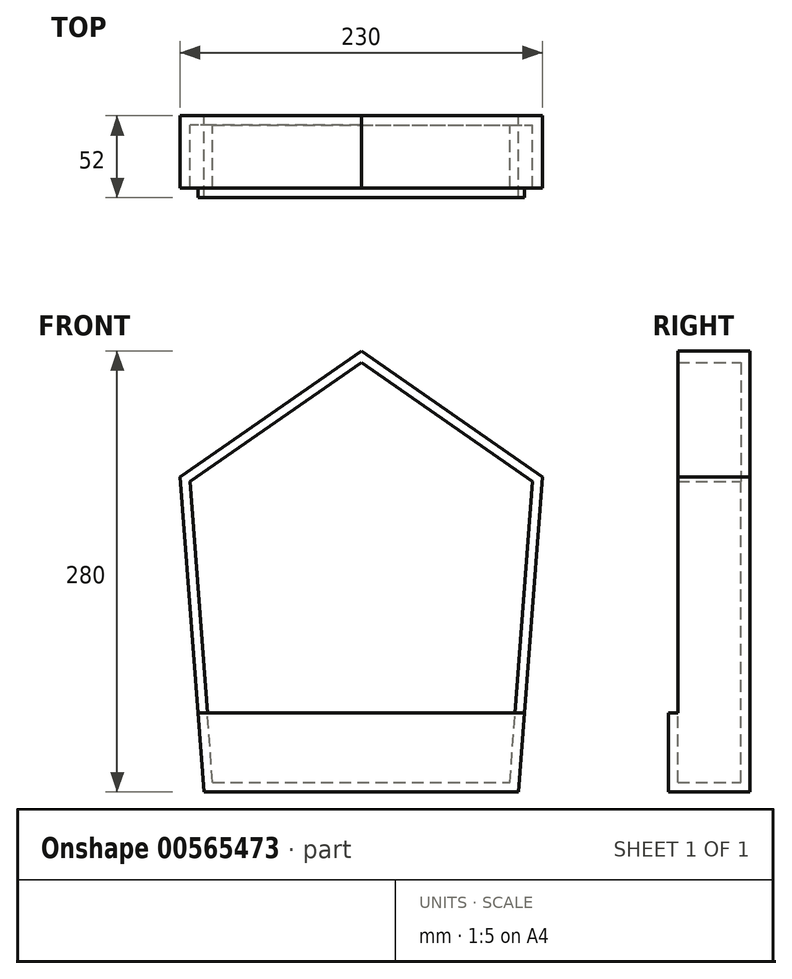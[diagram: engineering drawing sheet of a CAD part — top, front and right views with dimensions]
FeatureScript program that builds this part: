
annotation { "Feature Type Name" : "Feature", "Feature Type Description" : "" }
export const myFeature = defineFeature(function(context is Context, id is Id, definition is map)
    precondition{}
    {
        {
            var Q0;
            Q0=qCreatedBy(makeId("Front.planeOp"),FACE);
            var sketch = newSketch(context, id + "F0", { "sketchPlane" : qUnion([Q0])});
            skLineSegment(sketch, "E0.bottom", {"start": v(0, 0) * mm, "end": v(200, 0) * mm});
            skLineSegment(sketch, "E0.top", {"start": v(-15, 200) * mm, "end": v(215, 200) * mm});
            skLineSegment(sketch, "E0.left", {"start": v(0, 0) * mm, "end": v(-15, 200) * mm});
            skLineSegment(sketch, "E0.right", {"start": v(200, 0) * mm, "end": v(215, 200) * mm});
            skLineSegment(sketch, "E1", {"start": v(-15, 200) * mm, "end": v(100, 200) * mm});
            skLineSegment(sketch, "E2", {"start": v(100, 200) * mm, "end": v(100, 280) * mm});
            skLineSegment(sketch, "E3", {"start": v(100, 280) * mm, "end": v(-15, 200) * mm});
            skLineSegment(sketch, "E4", {"start": v(100, 280) * mm, "end": v(215, 200) * mm});
            skLineSegment(sketch, "E5", {"start": v(0, 0) * mm, "end": v(100, 0) * mm});
            skLineSegment(sketch, "E6", {"start": v(100, 0) * mm, "end": v(100, 200) * mm});
            skSolve(sketch);
        }
        {
            var Q0;
            Q0=makeQuery(id+"F0.imprint","IMPRINT",FACE,{"disambiguationData":[TD([[makeQuery(id+"F0.imprint","IMPRINT",EDGE,{"derivedFrom":sQuery(id+"F0.wireOp",EDGE,"E0.left")}),-1.0]])]});
            var Q1;
            Q1=makeQuery(id+"F0.imprint","IMPRINT",FACE,{"disambiguationData":[TD([[makeQuery(id+"F0.imprint","IMPRINT",EDGE,{"derivedFrom":sQuery(id+"F0.wireOp",EDGE,"E0.bottom")}),1.0]])]});
            var Q2;
            Q2=makeQuery(id+"F0.imprint","IMPRINT",FACE,{"disambiguationData":[TD([[makeQuery(id+"F0.imprint","IMPRINT",EDGE,{"derivedFrom":sQuery(id+"F0.wireOp",EDGE,"E0.top")}),1.0]])]});
            var Q3;
            Q3=makeQuery(id+"F0.imprint","IMPRINT",FACE,{"disambiguationData":[TD([[makeQuery(id+"F0.imprint","IMPRINT",EDGE,{"derivedFrom":sQuery(id+"F0.wireOp",EDGE,"E1")}),1.0]])]});
            extrude(context, id + "F1", {"entities" : qUnion([Q0, Q1, Q2, Q3]), "depth" : 6 * mm, "offsetDistance" : 25 * mm});
        }
        {
            var Q0;
            Q0=makeQuery(id+"F1.opExtrude","CAP_FACE",FACE,{"disambiguationData":[OSD([sQuery(id+"F0.wireOp",EDGE,"E0.bottom"),sQuery(id+"F0.wireOp",EDGE,"E0.left"),sQuery(id+"F0.wireOp",EDGE,"E0.right"),sQuery(id+"F0.wireOp",EDGE,"E3"),sQuery(id+"F0.wireOp",EDGE,"E4"),sQuery(id+"F0.wireOp",EDGE,"E5")])],"isStart":false});
            var sketch = newSketch(context, id + "F2", { "sketchPlane" : qUnion([Q0])});
            skLineSegment(sketch, "E7.0", {"start": v(100, 272.7) * mm, "end": v(-8.76, 197.03) * mm});
            skLineSegment(sketch, "E7.1", {"start": v(5.57, 6) * mm, "end": v(-8.76, 197.03) * mm});
            skLineSegment(sketch, "E7.2", {"start": v(100, 272.7) * mm, "end": v(208.76, 197.03) * mm});
            skLineSegment(sketch, "E7.3", {"start": v(194.43, 6) * mm, "end": v(208.76, 197.03) * mm});
            skLineSegment(sketch, "E7.4", {"start": v(5.57, 6) * mm, "end": v(194.43, 6) * mm});
            skSolve(sketch);
        }
        {
            var Q0;
            Q0=makeQuery(id+"F2.imprint","IMPRINT",FACE,{"disambiguationData":[TD([[makeQuery(id+"F2.imprint","IMPRINT",EDGE,{"derivedFrom":sQuery(id+"F2.wireOp",EDGE,"E7.0")}),-1.0]])]});
            extrude(context, id + "F3", {"entities" : qUnion([Q0]), "operationType" : NewBodyOperationType.ADD, "depth" : 40 * mm, "offsetDistance" : 25 * mm});
        }
        {
            var Q0;
            Q0=makeQuery(id+"F3.opExtrude","CAP_FACE",FACE,{"disambiguationData":[OSD([sQuery(id+"F0.wireOp",EDGE,"E0.bottom"),sQuery(id+"F0.wireOp",EDGE,"E0.left"),sQuery(id+"F0.wireOp",EDGE,"E0.right"),sQuery(id+"F0.wireOp",EDGE,"E3"),sQuery(id+"F0.wireOp",EDGE,"E4"),sQuery(id+"F0.wireOp",EDGE,"E5"),sQuery(id+"F2.wireOp",EDGE,"E7.0"),sQuery(id+"F2.wireOp",EDGE,"E7.1"),sQuery(id+"F2.wireOp",EDGE,"E7.2"),sQuery(id+"F2.wireOp",EDGE,"E7.3"),sQuery(id+"F2.wireOp",EDGE,"E7.4")])],"isStart":false});
            var sketch = newSketch(context, id + "F4", { "sketchPlane" : qUnion([Q0])});
            skLineSegment(sketch, "E8", {"start": v(-3.75, 50) * mm, "end": v(203.75, 50) * mm});
            skLineSegment(sketch, "E9", {"start": v(-3.75, 50) * mm, "end": v(0, 0) * mm});
            skLineSegment(sketch, "E10", {"start": v(0, 0) * mm, "end": v(200, 0) * mm});
            skLineSegment(sketch, "E11", {"start": v(200, 0) * mm, "end": v(203.75, 50) * mm});
            skSolve(sketch);
        }
        {
            var Q0;
            {var subQ5=makeQuery(id+"F3.opExtrude","CAP_EDGE",EDGE,{"disambiguationData":[OSD([sQuery(id+"F2.wireOp",EDGE,"E7.4")])],"isStart":false});Q0=makeQuery(id+"F4.imprint","IMPRINT",FACE,{"disambiguationData":[TD([[makeQuery(id+"F4.imprint","IMPRINT",EDGE,{"derivedFrom":subQ5}),1.0]])]});}
            var Q1;
            {var subQ0=sQuery(id+"F4.wireOp",EDGE,"E9");Q1=makeQuery(id+"F4.imprint","IMPRINT",FACE,{"disambiguationData":[TD([[makeQuery(id+"F4.imprint","IMPRINT",EDGE,{"derivedFrom":subQ0}),-1.0]])]});}
            extrude(context, id + "F5", {"entities" : qUnion([Q0, Q1]), "operationType" : NewBodyOperationType.ADD, "depth" : 6 * mm, "offsetDistance" : 25 * mm});
        }
    });
